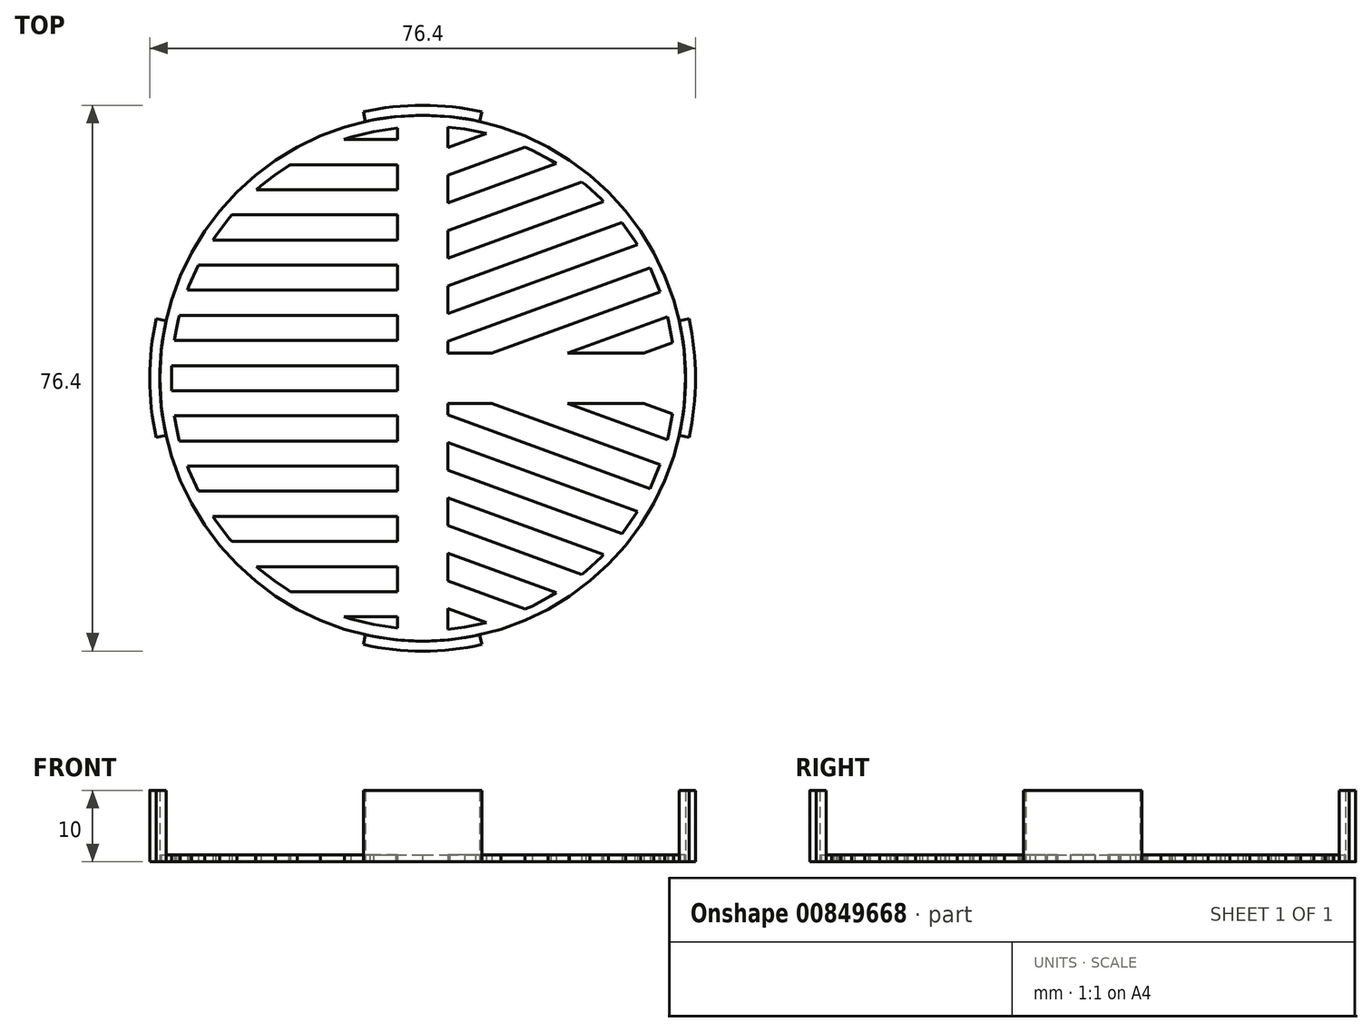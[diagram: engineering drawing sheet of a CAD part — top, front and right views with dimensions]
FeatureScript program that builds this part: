
annotation { "Feature Type Name" : "Feature", "Feature Type Description" : "" }
export const myFeature = defineFeature(function(context is Context, id is Id, definition is map)
    precondition{}
    {
        {
            var Q0;
            Q0=qCreatedBy(makeId("Top.planeOp"),FACE);
            var sketch = newSketch(context, id + "F0", { "sketchPlane" : qUnion([Q0])});
            skLineSegment(sketch, "E0", {"start": v(-10.98, -33.4) * mm, "end": v(-10.04, -33.7) * mm});
            skLineSegment(sketch, "E1", {"start": v(-10.04, -33.7) * mm, "end": v(-6.87, -34.49) * mm});
            skLineSegment(sketch, "E2", {"start": v(-6.87, -34.49) * mm, "end": v(-3.6, -34.98) * mm});
            skLineSegment(sketch, "E3", {"start": v(-3.6, -34.98) * mm, "end": v(-3.52, -34.98) * mm});
            skLineSegment(sketch, "E4", {"start": v(-3.52, -34.98) * mm, "end": v(-3.52, -33.4) * mm});
            skLineSegment(sketch, "E5", {"start": v(-3.52, -33.4) * mm, "end": v(-10.98, -33.4) * mm});
            skLineSegment(sketch, "E6", {"start": v(3.52, -32.25) * mm, "end": v(3.52, -35.16) * mm});
            skLineSegment(sketch, "E7", {"start": v(3.52, -35.16) * mm, "end": v(5.85, -34.86) * mm});
            skLineSegment(sketch, "E8", {"start": v(5.85, -34.86) * mm, "end": v(8.13, -34.4) * mm});
            skLineSegment(sketch, "E9", {"start": v(8.13, -34.4) * mm, "end": v(8.9, -34.21) * mm});
            skLineSegment(sketch, "E10", {"start": v(8.9, -34.21) * mm, "end": v(3.52, -32.25) * mm});
            skLineSegment(sketch, "E11", {"start": v(-23.24, -26.37) * mm, "end": v(-22.6, -26.93) * mm});
            skLineSegment(sketch, "E12", {"start": v(-22.6, -26.93) * mm, "end": v(-20.74, -28.4) * mm});
            skLineSegment(sketch, "E13", {"start": v(-20.74, -28.4) * mm, "end": v(-18.77, -29.73) * mm});
            skLineSegment(sketch, "E14", {"start": v(-18.77, -29.73) * mm, "end": v(-18.52, -29.88) * mm});
            skLineSegment(sketch, "E15", {"start": v(-18.52, -29.88) * mm, "end": v(-3.52, -29.88) * mm});
            skLineSegment(sketch, "E16", {"start": v(-3.52, -29.88) * mm, "end": v(-3.52, -26.37) * mm});
            skLineSegment(sketch, "E17", {"start": v(-3.52, -26.37) * mm, "end": v(-23.24, -26.37) * mm});
            skLineSegment(sketch, "E18", {"start": v(3.52, -24.51) * mm, "end": v(3.52, -28.38) * mm});
            skLineSegment(sketch, "E19", {"start": v(3.52, -28.38) * mm, "end": v(14.35, -32.33) * mm});
            skLineSegment(sketch, "E20", {"start": v(14.35, -32.33) * mm, "end": v(15.3, -31.9) * mm});
            skLineSegment(sketch, "E21", {"start": v(15.3, -31.9) * mm, "end": v(17.96, -30.48) * mm});
            skLineSegment(sketch, "E22", {"start": v(17.96, -30.48) * mm, "end": v(18.7, -30.03) * mm});
            skLineSegment(sketch, "E23", {"start": v(18.7, -30.03) * mm, "end": v(3.52, -24.51) * mm});
            skLineSegment(sketch, "E24", {"start": v(-29.36, -19.34) * mm, "end": v(-28.98, -19.92) * mm});
            skLineSegment(sketch, "E25", {"start": v(-28.98, -19.92) * mm, "end": v(-27.06, -22.44) * mm});
            skLineSegment(sketch, "E26", {"start": v(-27.06, -22.44) * mm, "end": v(-26.7, -22.85) * mm});
            skLineSegment(sketch, "E27", {"start": v(-26.7, -22.85) * mm, "end": v(-3.52, -22.85) * mm});
            skLineSegment(sketch, "E28", {"start": v(-3.52, -22.85) * mm, "end": v(-3.52, -19.34) * mm});
            skLineSegment(sketch, "E29", {"start": v(-3.52, -19.34) * mm, "end": v(-29.36, -19.34) * mm});
            skLineSegment(sketch, "E30", {"start": v(3.52, -16.77) * mm, "end": v(3.52, -20.64) * mm});
            skLineSegment(sketch, "E31", {"start": v(3.52, -20.64) * mm, "end": v(22.29, -27.47) * mm});
            skLineSegment(sketch, "E32", {"start": v(22.29, -27.47) * mm, "end": v(22.83, -27.04) * mm});
            skLineSegment(sketch, "E33", {"start": v(22.83, -27.04) * mm, "end": v(25.02, -25.02) * mm});
            skLineSegment(sketch, "E34", {"start": v(25.02, -25.02) * mm, "end": v(25.32, -24.7) * mm});
            skLineSegment(sketch, "E35", {"start": v(25.32, -24.7) * mm, "end": v(3.52, -16.77) * mm});
            skLineSegment(sketch, "E36", {"start": v(-32.94, -12.3) * mm, "end": v(-32.72, -12.9) * mm});
            skLineSegment(sketch, "E37", {"start": v(-32.72, -12.9) * mm, "end": v(-31.4, -15.82) * mm});
            skLineSegment(sketch, "E38", {"start": v(-31.4, -15.82) * mm, "end": v(-31.4, -15.82) * mm});
            skLineSegment(sketch, "E39", {"start": v(-31.4, -15.82) * mm, "end": v(-3.52, -15.82) * mm});
            skLineSegment(sketch, "E40", {"start": v(-3.52, -15.82) * mm, "end": v(-3.52, -12.3) * mm});
            skLineSegment(sketch, "E41", {"start": v(-3.52, -12.3) * mm, "end": v(-32.94, -12.3) * mm});
            skLineSegment(sketch, "E42", {"start": v(3.52, -9.02) * mm, "end": v(3.52, -12.9) * mm});
            skLineSegment(sketch, "E43", {"start": v(3.52, -12.9) * mm, "end": v(27.9, -21.77) * mm});
            skLineSegment(sketch, "E44", {"start": v(27.9, -21.77) * mm, "end": v(27.97, -21.67) * mm});
            skLineSegment(sketch, "E45", {"start": v(27.97, -21.67) * mm, "end": v(29.7, -19.23) * mm});
            skLineSegment(sketch, "E46", {"start": v(29.7, -19.23) * mm, "end": v(30.04, -18.68) * mm});
            skLineSegment(sketch, "E47", {"start": v(30.04, -18.68) * mm, "end": v(3.52, -9.02) * mm});
            skLineSegment(sketch, "E48", {"start": v(-34.76, -5.27) * mm, "end": v(-34.53, -6.65) * mm});
            skLineSegment(sketch, "E49", {"start": v(-34.53, -6.65) * mm, "end": v(-34.18, -8.26) * mm});
            skLineSegment(sketch, "E50", {"start": v(-34.18, -8.26) * mm, "end": v(-34.04, -8.79) * mm});
            skLineSegment(sketch, "E51", {"start": v(-34.04, -8.79) * mm, "end": v(-3.52, -8.79) * mm});
            skLineSegment(sketch, "E52", {"start": v(-3.52, -8.79) * mm, "end": v(-3.52, -5.27) * mm});
            skLineSegment(sketch, "E53", {"start": v(-3.52, -5.27) * mm, "end": v(-34.76, -5.27) * mm});
            skLineSegment(sketch, "E54", {"start": v(20.3, -3.52) * mm, "end": v(34.28, -8.6) * mm});
            skLineSegment(sketch, "E55", {"start": v(34.28, -8.6) * mm, "end": v(34.4, -8.13) * mm});
            skLineSegment(sketch, "E56", {"start": v(34.4, -8.13) * mm, "end": v(34.97, -5.08) * mm});
            skLineSegment(sketch, "E57", {"start": v(34.97, -5.08) * mm, "end": v(34.98, -4.99) * mm});
            skLineSegment(sketch, "E58", {"start": v(34.98, -4.99) * mm, "end": v(30.94, -3.52) * mm});
            skLineSegment(sketch, "E59", {"start": v(30.94, -3.52) * mm, "end": v(20.3, -3.52) * mm});
            skLineSegment(sketch, "E60", {"start": v(3.52, -3.52) * mm, "end": v(3.52, -5.15) * mm});
            skLineSegment(sketch, "E61", {"start": v(3.52, -5.15) * mm, "end": v(31.82, -15.45) * mm});
            skLineSegment(sketch, "E62", {"start": v(31.82, -15.45) * mm, "end": v(31.9, -15.3) * mm});
            skLineSegment(sketch, "E63", {"start": v(31.9, -15.3) * mm, "end": v(33.08, -12.52) * mm});
            skLineSegment(sketch, "E64", {"start": v(33.08, -12.52) * mm, "end": v(33.23, -12.1) * mm});
            skLineSegment(sketch, "E65", {"start": v(33.23, -12.1) * mm, "end": v(9.66, -3.52) * mm});
            skLineSegment(sketch, "E66", {"start": v(9.66, -3.52) * mm, "end": v(3.52, -3.52) * mm});
            skLineSegment(sketch, "E67", {"start": v(-35.12, 1.76) * mm, "end": v(-35.12, 1.7) * mm});
            skLineSegment(sketch, "E68", {"start": v(-35.12, 1.7) * mm, "end": v(-35.16, 0) * mm});
            skLineSegment(sketch, "E69", {"start": v(-35.16, 0) * mm, "end": v(-35.12, -1.7) * mm});
            skLineSegment(sketch, "E70", {"start": v(-35.12, -1.7) * mm, "end": v(-35.12, -1.76) * mm});
            skLineSegment(sketch, "E71", {"start": v(-35.12, -1.76) * mm, "end": v(-3.52, -1.76) * mm});
            skLineSegment(sketch, "E72", {"start": v(-3.52, -1.76) * mm, "end": v(-3.52, 1.76) * mm});
            skLineSegment(sketch, "E73", {"start": v(-3.52, 1.76) * mm, "end": v(-35.12, 1.76) * mm});
            skLineSegment(sketch, "E74", {"start": v(34.28, 8.6) * mm, "end": v(20.3, 3.52) * mm});
            skLineSegment(sketch, "E75", {"start": v(20.3, 3.52) * mm, "end": v(30.94, 3.52) * mm});
            skLineSegment(sketch, "E76", {"start": v(30.94, 3.52) * mm, "end": v(34.98, 5) * mm});
            skLineSegment(sketch, "E77", {"start": v(34.98, 5) * mm, "end": v(34.97, 5.08) * mm});
            skLineSegment(sketch, "E78", {"start": v(34.97, 5.08) * mm, "end": v(34.4, 8.13) * mm});
            skLineSegment(sketch, "E79", {"start": v(34.4, 8.13) * mm, "end": v(34.28, 8.6) * mm});
            skLineSegment(sketch, "E80", {"start": v(-34.04, 8.79) * mm, "end": v(-34.18, 8.26) * mm});
            skLineSegment(sketch, "E81", {"start": v(-34.18, 8.26) * mm, "end": v(-34.53, 6.66) * mm});
            skLineSegment(sketch, "E82", {"start": v(-34.53, 6.66) * mm, "end": v(-34.76, 5.28) * mm});
            skLineSegment(sketch, "E83", {"start": v(-34.76, 5.28) * mm, "end": v(-3.52, 5.28) * mm});
            skLineSegment(sketch, "E84", {"start": v(-3.52, 5.28) * mm, "end": v(-3.52, 8.79) * mm});
            skLineSegment(sketch, "E85", {"start": v(-3.52, 8.79) * mm, "end": v(-34.04, 8.79) * mm});
            skLineSegment(sketch, "E86", {"start": v(31.82, 15.45) * mm, "end": v(3.52, 5.15) * mm});
            skLineSegment(sketch, "E87", {"start": v(3.52, 5.15) * mm, "end": v(3.52, 3.52) * mm});
            skLineSegment(sketch, "E88", {"start": v(3.52, 3.52) * mm, "end": v(9.66, 3.52) * mm});
            skLineSegment(sketch, "E89", {"start": v(9.66, 3.52) * mm, "end": v(33.23, 12.1) * mm});
            skLineSegment(sketch, "E90", {"start": v(33.23, 12.1) * mm, "end": v(33.08, 12.52) * mm});
            skLineSegment(sketch, "E91", {"start": v(33.08, 12.52) * mm, "end": v(31.9, 15.3) * mm});
            skLineSegment(sketch, "E92", {"start": v(31.9, 15.3) * mm, "end": v(31.82, 15.45) * mm});
            skLineSegment(sketch, "E93", {"start": v(-31.4, 15.82) * mm, "end": v(-31.4, 15.82) * mm});
            skLineSegment(sketch, "E94", {"start": v(-31.4, 15.82) * mm, "end": v(-32.72, 12.9) * mm});
            skLineSegment(sketch, "E95", {"start": v(-32.72, 12.9) * mm, "end": v(-32.94, 12.3) * mm});
            skLineSegment(sketch, "E96", {"start": v(-32.94, 12.3) * mm, "end": v(-3.52, 12.3) * mm});
            skLineSegment(sketch, "E97", {"start": v(-3.52, 12.3) * mm, "end": v(-3.52, 15.82) * mm});
            skLineSegment(sketch, "E98", {"start": v(-3.52, 15.82) * mm, "end": v(-31.4, 15.82) * mm});
            skLineSegment(sketch, "E99", {"start": v(27.9, 21.77) * mm, "end": v(3.52, 12.9) * mm});
            skLineSegment(sketch, "E100", {"start": v(3.52, 12.9) * mm, "end": v(3.52, 9.02) * mm});
            skLineSegment(sketch, "E101", {"start": v(3.52, 9.02) * mm, "end": v(30.04, 18.68) * mm});
            skLineSegment(sketch, "E102", {"start": v(30.04, 18.68) * mm, "end": v(29.7, 19.23) * mm});
            skLineSegment(sketch, "E103", {"start": v(29.7, 19.23) * mm, "end": v(27.97, 21.67) * mm});
            skLineSegment(sketch, "E104", {"start": v(27.97, 21.67) * mm, "end": v(27.9, 21.77) * mm});
            skLineSegment(sketch, "E105", {"start": v(-26.7, 22.85) * mm, "end": v(-27.06, 22.45) * mm});
            skLineSegment(sketch, "E106", {"start": v(-27.06, 22.45) * mm, "end": v(-28.98, 19.92) * mm});
            skLineSegment(sketch, "E107", {"start": v(-28.98, 19.92) * mm, "end": v(-29.36, 19.34) * mm});
            skLineSegment(sketch, "E108", {"start": v(-29.36, 19.34) * mm, "end": v(-3.52, 19.34) * mm});
            skLineSegment(sketch, "E109", {"start": v(-3.52, 19.34) * mm, "end": v(-3.52, 22.85) * mm});
            skLineSegment(sketch, "E110", {"start": v(-3.52, 22.85) * mm, "end": v(-26.7, 22.85) * mm});
            skLineSegment(sketch, "E111", {"start": v(22.29, 27.47) * mm, "end": v(3.52, 20.64) * mm});
            skLineSegment(sketch, "E112", {"start": v(3.52, 20.64) * mm, "end": v(3.52, 16.77) * mm});
            skLineSegment(sketch, "E113", {"start": v(3.52, 16.77) * mm, "end": v(25.32, 24.7) * mm});
            skLineSegment(sketch, "E114", {"start": v(25.32, 24.7) * mm, "end": v(25.02, 25.02) * mm});
            skLineSegment(sketch, "E115", {"start": v(25.02, 25.02) * mm, "end": v(22.83, 27.04) * mm});
            skLineSegment(sketch, "E116", {"start": v(22.83, 27.04) * mm, "end": v(22.29, 27.47) * mm});
            skLineSegment(sketch, "E117", {"start": v(-18.52, 29.89) * mm, "end": v(-18.77, 29.73) * mm});
            skLineSegment(sketch, "E118", {"start": v(-18.77, 29.73) * mm, "end": v(-20.74, 28.4) * mm});
            skLineSegment(sketch, "E119", {"start": v(-20.74, 28.4) * mm, "end": v(-22.6, 26.93) * mm});
            skLineSegment(sketch, "E120", {"start": v(-22.6, 26.93) * mm, "end": v(-23.24, 26.37) * mm});
            skLineSegment(sketch, "E121", {"start": v(-23.24, 26.37) * mm, "end": v(-3.52, 26.37) * mm});
            skLineSegment(sketch, "E122", {"start": v(-3.52, 26.37) * mm, "end": v(-3.52, 29.89) * mm});
            skLineSegment(sketch, "E123", {"start": v(-3.52, 29.89) * mm, "end": v(-18.52, 29.89) * mm});
            skLineSegment(sketch, "E124", {"start": v(14.35, 32.33) * mm, "end": v(3.52, 28.38) * mm});
            skLineSegment(sketch, "E125", {"start": v(3.52, 28.38) * mm, "end": v(3.52, 24.51) * mm});
            skLineSegment(sketch, "E126", {"start": v(3.52, 24.51) * mm, "end": v(18.7, 30.03) * mm});
            skLineSegment(sketch, "E127", {"start": v(18.7, 30.03) * mm, "end": v(17.96, 30.48) * mm});
            skLineSegment(sketch, "E128", {"start": v(17.96, 30.48) * mm, "end": v(15.3, 31.9) * mm});
            skLineSegment(sketch, "E129", {"start": v(15.3, 31.9) * mm, "end": v(14.35, 32.33) * mm});
            skLineSegment(sketch, "E130", {"start": v(-3.52, 34.98) * mm, "end": v(-3.6, 34.98) * mm});
            skLineSegment(sketch, "E131", {"start": v(-3.6, 34.98) * mm, "end": v(-6.87, 34.49) * mm});
            skLineSegment(sketch, "E132", {"start": v(-6.87, 34.49) * mm, "end": v(-10.04, 33.7) * mm});
            skLineSegment(sketch, "E133", {"start": v(-10.04, 33.7) * mm, "end": v(-10.98, 33.4) * mm});
            skLineSegment(sketch, "E134", {"start": v(-10.98, 33.4) * mm, "end": v(-3.52, 33.4) * mm});
            skLineSegment(sketch, "E135", {"start": v(-3.52, 33.4) * mm, "end": v(-3.52, 34.98) * mm});
            skLineSegment(sketch, "E136", {"start": v(3.52, 35.16) * mm, "end": v(3.52, 32.25) * mm});
            skLineSegment(sketch, "E137", {"start": v(3.52, 32.25) * mm, "end": v(8.9, 34.21) * mm});
            skLineSegment(sketch, "E138", {"start": v(8.9, 34.21) * mm, "end": v(8.13, 34.4) * mm});
            skLineSegment(sketch, "E139", {"start": v(8.13, 34.4) * mm, "end": v(5.85, 34.86) * mm});
            skLineSegment(sketch, "E140", {"start": v(5.85, 34.86) * mm, "end": v(3.52, 35.16) * mm});
            skLineSegment(sketch, "E141", {"start": v(0, 36.8) * mm, "end": v(3.76, 36.61) * mm});
            skLineSegment(sketch, "E142", {"start": v(3.76, 36.61) * mm, "end": v(7.42, 36.05) * mm});
            skLineSegment(sketch, "E143", {"start": v(7.42, 36.05) * mm, "end": v(10.94, 35.15) * mm});
            skLineSegment(sketch, "E144", {"start": v(10.94, 35.15) * mm, "end": v(14.32, 33.9) * mm});
            skLineSegment(sketch, "E145", {"start": v(14.32, 33.9) * mm, "end": v(17.54, 32.36) * mm});
            skLineSegment(sketch, "E146", {"start": v(17.54, 32.36) * mm, "end": v(20.58, 30.52) * mm});
            skLineSegment(sketch, "E147", {"start": v(20.58, 30.52) * mm, "end": v(23.4, 28.4) * mm});
            skLineSegment(sketch, "E148", {"start": v(23.4, 28.4) * mm, "end": v(26.02, 26.02) * mm});
            skLineSegment(sketch, "E149", {"start": v(26.02, 26.02) * mm, "end": v(28.4, 23.4) * mm});
            skLineSegment(sketch, "E150", {"start": v(28.4, 23.4) * mm, "end": v(30.52, 20.58) * mm});
            skLineSegment(sketch, "E151", {"start": v(30.52, 20.58) * mm, "end": v(32.36, 17.54) * mm});
            skLineSegment(sketch, "E152", {"start": v(32.36, 17.54) * mm, "end": v(33.9, 14.32) * mm});
            skLineSegment(sketch, "E153", {"start": v(33.9, 14.32) * mm, "end": v(35.14, 10.94) * mm});
            skLineSegment(sketch, "E154", {"start": v(35.14, 10.94) * mm, "end": v(36.05, 7.42) * mm});
            skLineSegment(sketch, "E155", {"start": v(36.05, 7.42) * mm, "end": v(36.61, 3.76) * mm});
            skLineSegment(sketch, "E156", {"start": v(36.61, 3.76) * mm, "end": v(36.8, 0) * mm});
            skLineSegment(sketch, "E157", {"start": v(36.8, 0) * mm, "end": v(36.61, -3.76) * mm});
            skLineSegment(sketch, "E158", {"start": v(36.61, -3.76) * mm, "end": v(36.05, -7.42) * mm});
            skLineSegment(sketch, "E159", {"start": v(36.05, -7.42) * mm, "end": v(35.14, -10.94) * mm});
            skLineSegment(sketch, "E160", {"start": v(35.14, -10.94) * mm, "end": v(33.9, -14.32) * mm});
            skLineSegment(sketch, "E161", {"start": v(33.9, -14.32) * mm, "end": v(32.36, -17.54) * mm});
            skLineSegment(sketch, "E162", {"start": v(32.36, -17.54) * mm, "end": v(30.52, -20.58) * mm});
            skLineSegment(sketch, "E163", {"start": v(30.52, -20.58) * mm, "end": v(28.4, -23.4) * mm});
            skLineSegment(sketch, "E164", {"start": v(28.4, -23.4) * mm, "end": v(26.02, -26.02) * mm});
            skLineSegment(sketch, "E165", {"start": v(26.02, -26.02) * mm, "end": v(23.4, -28.4) * mm});
            skLineSegment(sketch, "E166", {"start": v(23.4, -28.4) * mm, "end": v(20.58, -30.52) * mm});
            skLineSegment(sketch, "E167", {"start": v(20.58, -30.52) * mm, "end": v(17.54, -32.36) * mm});
            skLineSegment(sketch, "E168", {"start": v(17.54, -32.36) * mm, "end": v(14.32, -33.9) * mm});
            skLineSegment(sketch, "E169", {"start": v(14.32, -33.9) * mm, "end": v(10.94, -35.14) * mm});
            skLineSegment(sketch, "E170", {"start": v(10.94, -35.14) * mm, "end": v(7.42, -36.05) * mm});
            skLineSegment(sketch, "E171", {"start": v(7.42, -36.05) * mm, "end": v(3.76, -36.61) * mm});
            skLineSegment(sketch, "E172", {"start": v(3.76, -36.61) * mm, "end": v(0, -36.8) * mm});
            skLineSegment(sketch, "E173", {"start": v(0, -36.8) * mm, "end": v(-3.76, -36.61) * mm});
            skLineSegment(sketch, "E174", {"start": v(-3.76, -36.61) * mm, "end": v(-7.42, -36.05) * mm});
            skLineSegment(sketch, "E175", {"start": v(-7.42, -36.05) * mm, "end": v(-10.94, -35.14) * mm});
            skLineSegment(sketch, "E176", {"start": v(-10.94, -35.14) * mm, "end": v(-14.32, -33.9) * mm});
            skLineSegment(sketch, "E177", {"start": v(-14.32, -33.9) * mm, "end": v(-17.54, -32.36) * mm});
            skLineSegment(sketch, "E178", {"start": v(-17.54, -32.36) * mm, "end": v(-20.58, -30.52) * mm});
            skLineSegment(sketch, "E179", {"start": v(-20.58, -30.52) * mm, "end": v(-23.4, -28.4) * mm});
            skLineSegment(sketch, "E180", {"start": v(-23.4, -28.4) * mm, "end": v(-26.02, -26.02) * mm});
            skLineSegment(sketch, "E181", {"start": v(-26.02, -26.02) * mm, "end": v(-28.4, -23.4) * mm});
            skLineSegment(sketch, "E182", {"start": v(-28.4, -23.4) * mm, "end": v(-30.52, -20.58) * mm});
            skLineSegment(sketch, "E183", {"start": v(-30.52, -20.58) * mm, "end": v(-32.36, -17.54) * mm});
            skLineSegment(sketch, "E184", {"start": v(-32.36, -17.54) * mm, "end": v(-33.9, -14.32) * mm});
            skLineSegment(sketch, "E185", {"start": v(-33.9, -14.32) * mm, "end": v(-35.15, -10.94) * mm});
            skLineSegment(sketch, "E186", {"start": v(-35.15, -10.94) * mm, "end": v(-36.05, -7.42) * mm});
            skLineSegment(sketch, "E187", {"start": v(-36.05, -7.42) * mm, "end": v(-36.61, -3.76) * mm});
            skLineSegment(sketch, "E188", {"start": v(-36.61, -3.76) * mm, "end": v(-36.8, 0) * mm});
            skLineSegment(sketch, "E189", {"start": v(-36.8, 0) * mm, "end": v(-36.61, 3.76) * mm});
            skLineSegment(sketch, "E190", {"start": v(-36.61, 3.76) * mm, "end": v(-36.05, 7.42) * mm});
            skLineSegment(sketch, "E191", {"start": v(-36.05, 7.42) * mm, "end": v(-35.15, 10.94) * mm});
            skLineSegment(sketch, "E192", {"start": v(-35.15, 10.94) * mm, "end": v(-33.9, 14.32) * mm});
            skLineSegment(sketch, "E193", {"start": v(-33.9, 14.32) * mm, "end": v(-32.36, 17.54) * mm});
            skLineSegment(sketch, "E194", {"start": v(-32.36, 17.54) * mm, "end": v(-30.52, 20.58) * mm});
            skLineSegment(sketch, "E195", {"start": v(-30.52, 20.58) * mm, "end": v(-28.4, 23.4) * mm});
            skLineSegment(sketch, "E196", {"start": v(-28.4, 23.4) * mm, "end": v(-26.02, 26.02) * mm});
            skLineSegment(sketch, "E197", {"start": v(-26.02, 26.02) * mm, "end": v(-23.4, 28.4) * mm});
            skLineSegment(sketch, "E198", {"start": v(-23.4, 28.4) * mm, "end": v(-20.58, 30.52) * mm});
            skLineSegment(sketch, "E199", {"start": v(-20.58, 30.52) * mm, "end": v(-17.54, 32.36) * mm});
            skLineSegment(sketch, "E200", {"start": v(-17.54, 32.36) * mm, "end": v(-14.32, 33.9) * mm});
            skLineSegment(sketch, "E201", {"start": v(-14.32, 33.9) * mm, "end": v(-10.94, 35.15) * mm});
            skLineSegment(sketch, "E202", {"start": v(-10.94, 35.15) * mm, "end": v(-7.42, 36.05) * mm});
            skLineSegment(sketch, "E203", {"start": v(-7.42, 36.05) * mm, "end": v(-3.76, 36.61) * mm});
            skLineSegment(sketch, "E204", {"start": v(-3.76, 36.61) * mm, "end": v(0, 36.8) * mm});
            skSolve(sketch);
        }
        {
            var Q0;
            Q0 = qSketchRegion(id + "F0", true);
            extrude(context, id + "F1", {"entities" : qUnion([Q0]), "depth" : 1 * mm, "offsetDistance" : 25 * mm});
        }
        {
            var Q0;
            Q0=qCreatedBy(makeId("Top.planeOp"),FACE);
            var sketch = newSketch(context, id + "F2", { "sketchPlane" : qUnion([Q0])});
            skArc(sketch, "E205", {"start": v(-8, 35.92) * mm, "mid": v(0, 36.8) * mm, "end": v(8, 35.92) * mm});
            skArc(sketch, "E206", {"start": v(35.92, 8) * mm, "mid": v(36.8, 0) * mm, "end": v(35.92, -8) * mm});
            skArc(sketch, "E207", {"start": v(8, -35.92) * mm, "mid": v(0, -36.8) * mm, "end": v(-8, -35.92) * mm});
            skArc(sketch, "E208.0", {"start": v(-8.3, 37.29) * mm, "mid": v(0, 38.2) * mm, "end": v(8.3, 37.29) * mm});
            skArc(sketch, "E209.0", {"start": v(37.29, 8.3) * mm, "mid": v(38.2, 0) * mm, "end": v(37.29, -8.3) * mm});
            skArc(sketch, "E210.0", {"start": v(8.3, -37.29) * mm, "mid": v(0, -38.2) * mm, "end": v(-8.3, -37.29) * mm});
            skLineSegment(sketch, "E211", {"start": v(35.92, 8) * mm, "end": v(37.29, 8.3) * mm});
            skLineSegment(sketch, "E212", {"start": v(35.92, -8) * mm, "end": v(37.29, -8.3) * mm});
            skLineSegment(sketch, "E213", {"start": v(8, 35.92) * mm, "end": v(8.3, 37.29) * mm});
            skLineSegment(sketch, "E214", {"start": v(-8, 35.92) * mm, "end": v(-8.3, 37.29) * mm});
            skLineSegment(sketch, "E215", {"start": v(8, -35.92) * mm, "end": v(8.3, -37.29) * mm});
            skLineSegment(sketch, "E216", {"start": v(-8, -35.92) * mm, "end": v(-8.3, -37.29) * mm});
            skLineSegment(sketch, "E217", {"start": v(-35.92, -8) * mm, "end": v(0, 0) * mm, "construction": true});
            skLineSegment(sketch, "E218", {"start": v(35.92, -8) * mm, "end": v(0, 0) * mm, "construction": true});
            skLineSegment(sketch, "E219", {"start": v(-35.92, 8) * mm, "end": v(0, 0) * mm, "construction": true});
            skLineSegment(sketch, "E220", {"start": v(0, 0) * mm, "end": v(35.92, 8) * mm, "construction": true});
            skArc(sketch, "E221", {"start": v(-35.92, -8) * mm, "mid": v(-36.8, 0) * mm, "end": v(-35.92, 8) * mm});
            skArc(sketch, "E222.0", {"start": v(-37.29, -8.3) * mm, "mid": v(-38.2, 0) * mm, "end": v(-37.29, 8.3) * mm});
            skLineSegment(sketch, "E223", {"start": v(-37.29, 8.3) * mm, "end": v(-35.92, 8) * mm});
            skLineSegment(sketch, "E224", {"start": v(-37.29, -8.3) * mm, "end": v(-35.92, -8) * mm});
            skSolve(sketch);
        }
        {
            var Q0;
            Q0 = qSketchRegion(id + "F2", true);
            extrude(context, id + "F3", {"entities" : qUnion([Q0]), "depth" : 10 * mm, "offsetDistance" : 25 * mm});
        }
    });
